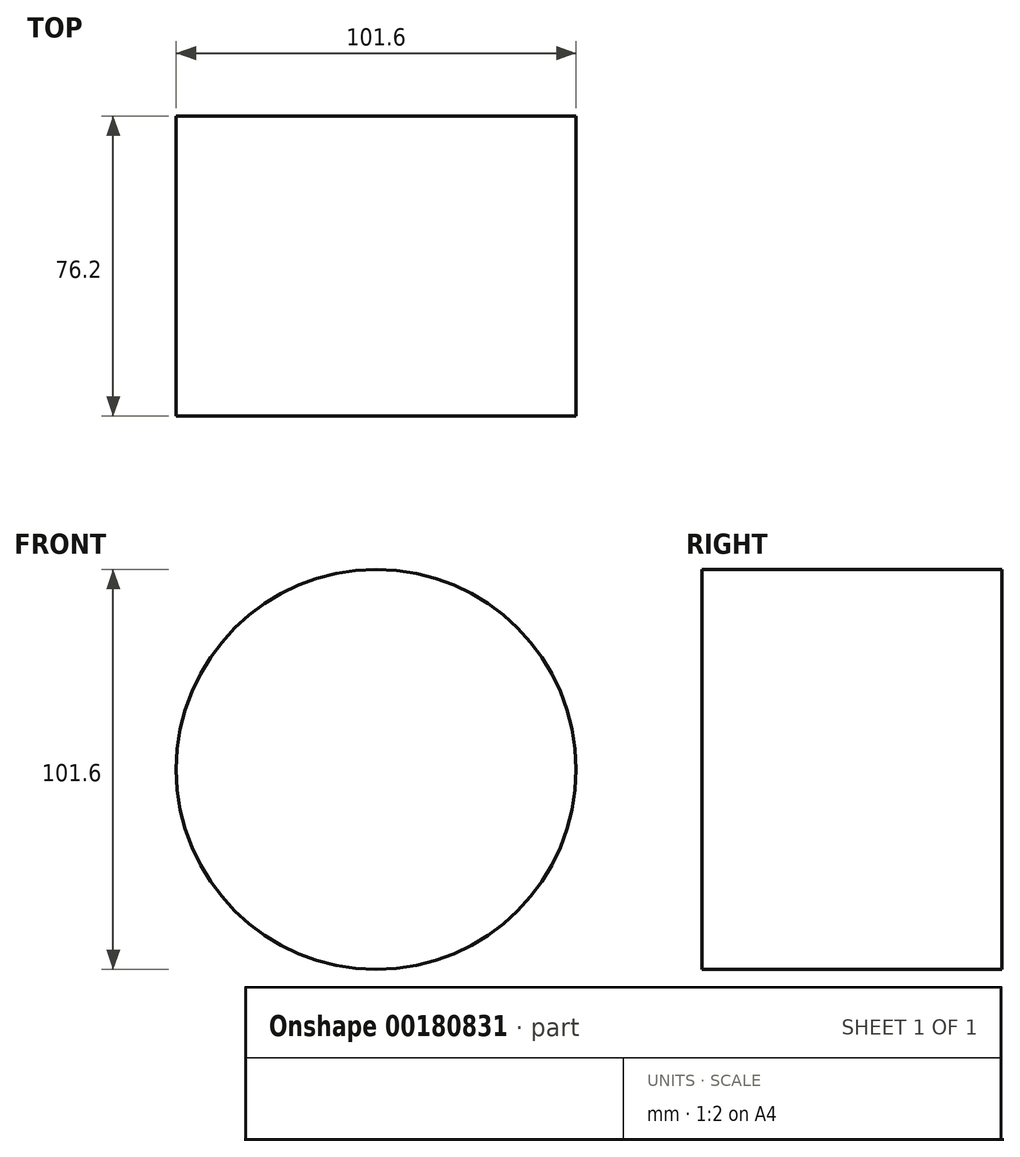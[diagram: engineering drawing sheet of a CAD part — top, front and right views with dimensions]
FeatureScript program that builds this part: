
annotation { "Feature Type Name" : "Feature", "Feature Type Description" : "" }
export const myFeature = defineFeature(function(context is Context, id is Id, definition is map)
    precondition{}
    {
        {
            var Q0;
            Q0=qCreatedBy(makeId("Front.planeOp"),FACE);
            var sketch = newSketch(context, id + "F0", { "sketchPlane" : qUnion([Q0])});
            skCircle(sketch, "E0", {"center": v(-68.8, 38.08) * mm, "radius": 50.8 * mm});
            skSolve(sketch);
        }
        {
            var Q0;
            Q0 = qSketchRegion(id + "F0", true);
            extrude(context, id + "F1", {"entities" : qUnion([Q0]), "depth" : 76.2 * mm});
        }
    });
